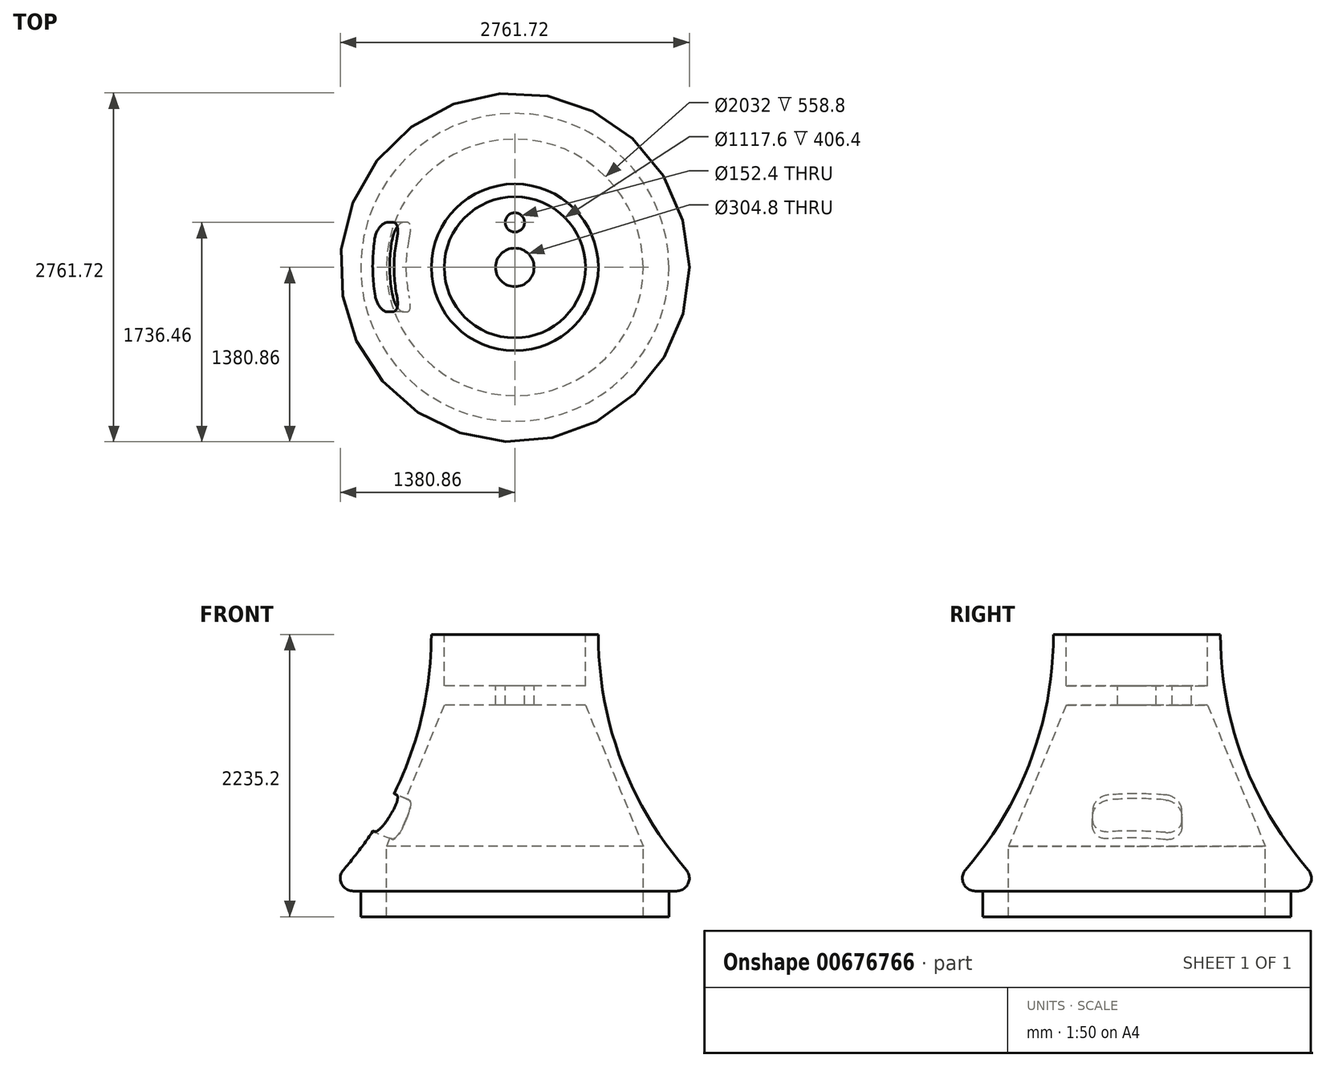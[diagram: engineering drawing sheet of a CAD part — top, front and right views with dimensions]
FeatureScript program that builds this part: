
annotation { "Feature Type Name" : "Feature", "Feature Type Description" : "" }
export const myFeature = defineFeature(function(context is Context, id is Id, definition is map)
    precondition{}
    {
        {
            var Q0;
            Q0=qCreatedBy(makeId("Front.planeOp"),FACE);
            var sketch = newSketch(context, id + "F0", { "sketchPlane" : qUnion([Q0])});
            skLineSegment(sketch, "E0", {"start": v(-558.8, 0) * mm, "end": v(-660.4, 0) * mm});
            skArc(sketch, "E1", {"start": v(-1356.01, -1863.83) * mm, "mid": v(-839.97, -994.7) * mm, "end": v(-660.4, 0) * mm});
            skLineSegment(sketch, "E2", {"start": v(0, -406.4) * mm, "end": v(0, -558.8) * mm});
            skLineSegment(sketch, "E3", {"start": v(-558.8, 0) * mm, "end": v(-558.8, -406.4) * mm});
            skPoint(sketch, "E4.orphan", {"position": v(0, 0) * mm});
            skLineSegment(sketch, "E5", {"start": v(-558.8, -406.4) * mm, "end": v(-558.8, -558.8) * mm});
            skLineSegment(sketch, "E6", {"start": v(-1016, -2235.2) * mm, "end": v(-1219.2, -2235.2) * mm});
            skLineSegment(sketch, "E7", {"start": v(-1016, -2235.2) * mm, "end": v(-1016, -1676.4) * mm});
            skLineSegment(sketch, "E8", {"start": v(-1219.2, -2235.2) * mm, "end": v(-1219.2, -2032) * mm});
            skLineSegment(sketch, "E9", {"start": v(-1219.2, -2032) * mm, "end": v(-1279.26, -2032) * mm});
            skLineSegment(sketch, "E10", {"start": v(-558.8, -558.8) * mm, "end": v(-1016, -1676.4) * mm});
            skPoint(sketch, "E11.visualSharp", {"position": v(-1514.25, -2032) * mm});
            skArc(sketch, "E11.filletArc", {"start": v(-1356.01, -1863.83) * mm, "mid": v(-1371.68, -1972.59) * mm, "end": v(-1279.26, -2032) * mm});
            skLineSegment(sketch, "E12", {"start": v(-558.8, -558.8) * mm, "end": v(0, -558.8) * mm});
            skLineSegment(sketch, "E13", {"start": v(0, -406.4) * mm, "end": v(-558.8, -406.4) * mm});
            skPoint(sketch, "E14.orphan", {"position": v(0, -2235.2) * mm});
            skLineSegment(sketch, "E15", {"start": v(-1016, -1676.4) * mm, "end": v(-1163.89, -1615.9) * mm});
            skSolve(sketch);
        }
        {
            var Q0;
            Q0 = qSketchRegion(id + "F0", true);
            var Q1;
            Q1=sQuery(id+"F0.wireOp",EDGE,"E2");
            revolve(context, id + "F1", {"entities" : qUnion([Q0]), "axis" : qUnion([Q1]), "revolveType" : RevolveType.FULL});
        }
        {
            var Q0;
            Q0=makeQuery(id+"F1.opRevolve","SWEPT_FACE",FACE,{"disambiguationData":[OSD([sQuery(id+"F0.wireOp",EDGE,"E13")])]});
            var sketch = newSketch(context, id + "F2", { "sketchPlane" : qUnion([Q0])});
            skCircle(sketch, "E16", {"center": v(0, 0) * mm, "radius": 152.4 * mm});
            skCircle(sketch, "E17", {"center": v(0, 355.6) * mm, "radius": 76.2 * mm});
            skSolve(sketch);
        }
        {
            var Q0;
            Q0 = qSketchRegion(id + "F2", true);
            extrude(context, id + "F3", {"entities" : qUnion([Q0]), "operationType" : NewBodyOperationType.REMOVE, "oppositeDirection" : true, "depth" : 152.4 * mm, "offsetDistance" : 25.4 * mm});
        }
        {
            var Q0;
            Q0=sQuery(id+"F0.wireOp",VERTEX,"E15.end");
            var Q1;
            Q1=sQuery(id+"F0.wireOp",EDGE,"E15");
            cPlane(context, id + "F4", {"entities" : qUnion([Q0, Q1]), "cplaneType" : CPlaneType.LINE_POINT, "offset" : 25.4 * mm, "width" : 152.4 * mm, "height" : 152.4 * mm});
        }
        {
            var Q0;
            Q0=qCreatedBy(id+"F4.planeOp",FACE);
            var sketch = newSketch(context, id + "F5", { "sketchPlane" : qUnion([Q0])});
            skPoint(sketch, "E18.0", {"position": v(0, -1936.28) * mm});
            skLineSegment(sketch, "E19.0", {"start": v(0, -2238.5) * mm, "end": v(0, -1936.28) * mm});
            skLineSegment(sketch, "E20", {"start": v(0, -1936.28) * mm, "end": v(-304.8, -1936.28) * mm});
            skLineSegment(sketch, "E21", {"start": v(-431.8, -1809.28) * mm, "end": v(-431.8, -1580.68) * mm});
            skLineSegment(sketch, "E22", {"start": v(-304.8, -1453.68) * mm, "end": v(304.8, -1453.68) * mm});
            skLineSegment(sketch, "E23", {"start": v(431.8, -1580.68) * mm, "end": v(431.8, -1809.28) * mm});
            skLineSegment(sketch, "E24", {"start": v(227.39, -1863.43) * mm, "end": v(-226.52, -1870.86) * mm});
            skLineSegment(sketch, "E25", {"start": v(352.3, -1734.36) * mm, "end": v(351, -1654.8) * mm});
            skLineSegment(sketch, "E26", {"start": v(224, -1529.88) * mm, "end": v(-228.6, -1529.88) * mm});
            skLineSegment(sketch, "E27", {"start": v(-355.6, -1656.88) * mm, "end": v(-355.6, -1743.88) * mm});
            skLineSegment(sketch, "E28.trimOffspring", {"start": v(0, -1867.15) * mm, "end": v(0, -1864.32) * mm});
            skLineSegment(sketch, "E29.trimOffspring", {"start": v(0, -1529.88) * mm, "end": v(0, -250.05) * mm});
            skPoint(sketch, "E30.visualSharp", {"position": v(-431.8, -1453.68) * mm});
            skArc(sketch, "E30.filletArc", {"start": v(-304.8, -1453.68) * mm, "mid": v(-394.6, -1490.88) * mm, "end": v(-431.8, -1580.68) * mm});
            skPoint(sketch, "E31.visualSharp", {"position": v(-431.8, -1936.28) * mm});
            skArc(sketch, "E31.filletArc", {"start": v(-431.8, -1809.28) * mm, "mid": v(-394.6, -1899.08) * mm, "end": v(-304.8, -1936.28) * mm});
            skArc(sketch, "E32.filletArc", {"start": v(304.8, -1936.28) * mm, "mid": v(394.6, -1899.08) * mm, "end": v(431.8, -1809.28) * mm});
            skLineSegment(sketch, "E33", {"start": v(0, -1936.28) * mm, "end": v(304.8, -1936.28) * mm});
            skPoint(sketch, "E34.visualSharp", {"position": v(354.37, -1861.35) * mm});
            skArc(sketch, "E34.filletArc", {"start": v(227.39, -1863.43) * mm, "mid": v(316.57, -1824.76) * mm, "end": v(352.3, -1734.36) * mm});
            skPoint(sketch, "E35.visualSharp", {"position": v(431.8, -1453.68) * mm});
            skArc(sketch, "E35.filletArc", {"start": v(431.8, -1580.68) * mm, "mid": v(394.6, -1490.88) * mm, "end": v(304.8, -1453.68) * mm});
            skPoint(sketch, "E36.visualSharp", {"position": v(-355.6, -1872.97) * mm});
            skArc(sketch, "E36.filletArc", {"start": v(-355.6, -1743.88) * mm, "mid": v(-317.66, -1834.41) * mm, "end": v(-226.52, -1870.86) * mm});
            skPoint(sketch, "E37.visualSharp", {"position": v(-355.6, -1529.88) * mm});
            skArc(sketch, "E37.filletArc", {"start": v(-228.6, -1529.88) * mm, "mid": v(-318.4, -1567.08) * mm, "end": v(-355.6, -1656.88) * mm});
            skPoint(sketch, "E38.visualSharp", {"position": v(348.94, -1529.88) * mm});
            skArc(sketch, "E38.filletArc", {"start": v(351, -1654.8) * mm, "mid": v(313.07, -1566.34) * mm, "end": v(224, -1529.88) * mm});
            skPoint(sketch, "E39.end.orphan", {"position": v(431.8, -1529.88) * mm});
            skSolve(sketch);
        }
        {
            var Q0;
            Q0=makeQuery(id+"F5.imprint","IMPRINT",FACE,{"disambiguationData":[TD([[makeQuery(id+"F5.imprint","IMPRINT",EDGE,{"derivedFrom":sQuery(id+"F5.wireOp",EDGE,"E25")}),1.0]])]});
            extrude(context, id + "F6", {"entities" : qUnion([Q0]), "operationType" : NewBodyOperationType.REMOVE, "oppositeDirection" : true, "depth" : 254 * mm, "offsetDistance" : 25.4 * mm});
        }
        {
            var Q0;
            Q0=sQuery(id+"F0.wireOp",EDGE,"E10");
            cPlane(context, id + "F7", {"entities" : qUnion([Q0]), "cplaneType" : CPlaneType.LINE_ANGLE, "offset" : 25.4 * mm, "angle" : 0 * degree, "width" : 152.4 * mm, "height" : 152.4 * mm});
        }
    });
